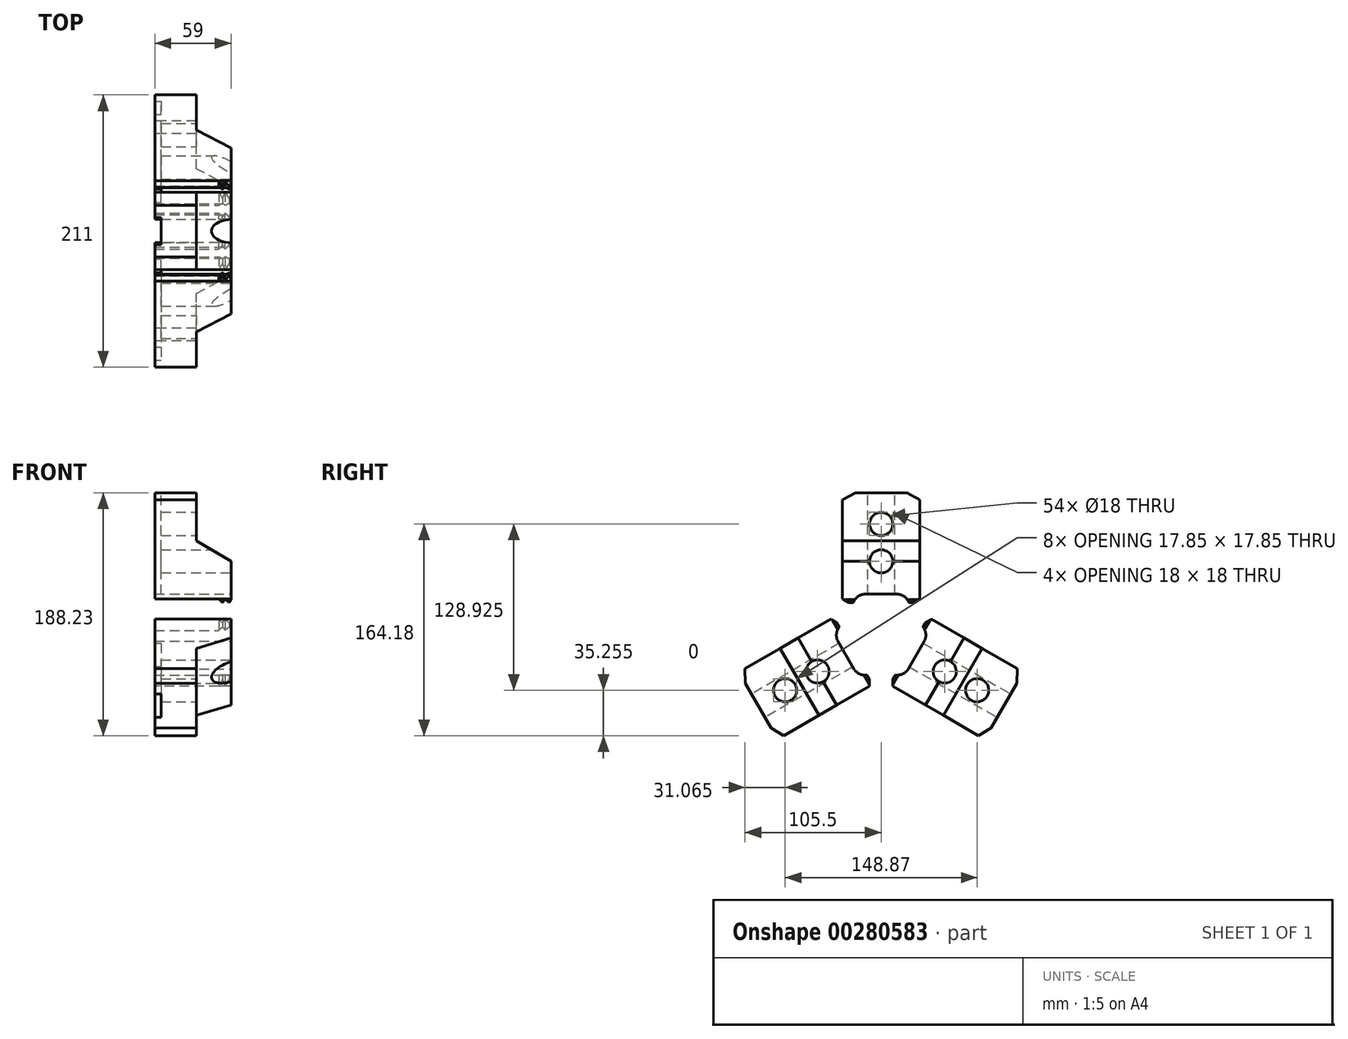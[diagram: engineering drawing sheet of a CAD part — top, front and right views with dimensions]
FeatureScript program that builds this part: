
annotation { "Feature Type Name" : "Feature", "Feature Type Description" : "" }
export const myFeature = defineFeature(function(context is Context, id is Id, definition is map)
    precondition{}
    {
        {
            var Q0;
            Q0=qCreatedBy(makeId("Right.planeOp"),FACE);
            var sketch = newSketch(context, id + "F0", { "sketchPlane" : qUnion([Q0])});
            skLineSegment(sketch, "E0", {"start": v(0, 137.35) * mm, "end": v(0, 0) * mm, "construction": true});
            skLineSegment(sketch, "E1", {"start": v(0, 25) * mm, "end": v(25, 25) * mm});
            skLineSegment(sketch, "E2", {"start": v(25, 25) * mm, "end": v(30, 27.7) * mm});
            skLineSegment(sketch, "E3", {"start": v(30, 27.7) * mm, "end": v(30, 104.5) * mm});
            skLineSegment(sketch, "E4", {"start": v(30, 104.5) * mm, "end": v(20, 110) * mm});
            skLineSegment(sketch, "E5", {"start": v(20, 110) * mm, "end": v(0, 110) * mm});
            skLineSegment(sketch, "E6", {"start": v(0, 110) * mm, "end": v(-20, 110) * mm});
            skLineSegment(sketch, "E7", {"start": v(-20, 110) * mm, "end": v(-30, 104.5) * mm});
            skLineSegment(sketch, "E8", {"start": v(-30, 104.5) * mm, "end": v(-30, 27.7) * mm});
            skLineSegment(sketch, "E9", {"start": v(-30, 27.7) * mm, "end": v(-25, 25) * mm});
            skLineSegment(sketch, "E10", {"start": v(-25, 25) * mm, "end": v(0, 25) * mm});
            skCircle(sketch, "E11", {"center": v(0, 0) * mm, "radius": 25 * mm, "construction": true});
            skSolve(sketch);
        }
        {
            var Q0;
            Q0 = qSketchRegion(id + "F0", true);
            extrude(context, id + "F1", {"entities" : qUnion([Q0]), "depth" : 62 * mm, "hasSecondDirection" : true, "secondDirectionOppositeDirection" : false, "secondDirectionDepth" : 3 * mm});
        }
        {
            var Q0;
            Q0=makeQuery(id+"F1.opExtrude","SWEPT_FACE",FACE,{"disambiguationData":[OSD([sQuery(id+"F0.wireOp",EDGE,"E8")])]});
            var sketch = newSketch(context, id + "F2", { "sketchPlane" : qUnion([Q0])});
            skLineSegment(sketch, "E12", {"start": v(35, 110) * mm, "end": v(35, 73) * mm});
            skLineSegment(sketch, "E13", {"start": v(35, 73) * mm, "end": v(62, 57) * mm});
            skLineSegment(sketch, "E14", {"start": v(62, 57) * mm, "end": v(62, 110) * mm});
            skLineSegment(sketch, "E15", {"start": v(62, 110) * mm, "end": v(35, 110) * mm});
            skLineSegment(sketch, "E16", {"start": v(3, 27.7) * mm, "end": v(52.5, 27.7) * mm});
            skLineSegment(sketch, "E17", {"start": v(52.5, 27.7) * mm, "end": v(55.5, 25) * mm});
            skLineSegment(sketch, "E18", {"start": v(55.5, 25) * mm, "end": v(57.5, 27.7) * mm});
            skLineSegment(sketch, "E19", {"start": v(57.5, 27.7) * mm, "end": v(60.5, 25) * mm});
            skLineSegment(sketch, "E20", {"start": v(60.5, 25) * mm, "end": v(62, 27) * mm});
            skLineSegment(sketch, "E21", {"start": v(62, 27) * mm, "end": v(62, 25) * mm});
            skLineSegment(sketch, "E22", {"start": v(62, 25) * mm, "end": v(3, 25) * mm});
            skLineSegment(sketch, "E23", {"start": v(3, 25) * mm, "end": v(3, 27.7) * mm});
            skSolve(sketch);
        }
        {
            var Q0;
            Q0 = qSketchRegion(id + "F2", true);
            var Q1;
            Q1=makeQuery(id+"F1.opExtrude","SWEPT_FACE",FACE,{"disambiguationData":[OSD([sQuery(id+"F0.wireOp",EDGE,"E3")])]});
            extrude(context, id + "F3", {"entities" : qUnion([Q0]), "operationType" : NewBodyOperationType.REMOVE, "endBound" : BoundingType.UP_TO_SURFACE, "oppositeDirection" : true, "endBoundEntityFace" : qUnion([Q1]), "depth" : 25 * mm});
        }
        {
            var Q0;
            Q0=makeQuery(id+"F1.opExtrude","SWEPT_FACE",FACE,{"disambiguationData":[OSD([sQuery(id+"F0.wireOp",EDGE,"E5"),sQuery(id+"F0.wireOp",EDGE,"E6")])]});
            var sketch = newSketch(context, id + "F4", { "sketchPlane" : qUnion([Q0])});
            skLineSegment(sketch, "E24", {"start": v(3, 0) * mm, "end": v(3, -10.5) * mm});
            skLineSegment(sketch, "E25", {"start": v(3, -10.5) * mm, "end": v(8, -10.5) * mm});
            skLineSegment(sketch, "E26", {"start": v(8, -10.5) * mm, "end": v(8, 0) * mm});
            skLineSegment(sketch, "E27", {"start": v(8, 0) * mm, "end": v(8, 10.5) * mm});
            skLineSegment(sketch, "E28", {"start": v(8, 10.5) * mm, "end": v(3, 10.5) * mm});
            skLineSegment(sketch, "E29", {"start": v(3, 10.5) * mm, "end": v(3, 0) * mm});
            skSolve(sketch);
        }
        {
            var Q0;
            Q0=makeQuery(id+"F4.imprint","IMPRINT",FACE,{"disambiguationData":[TD([[makeQuery(id+"F4.imprint","IMPRINT",EDGE,{"derivedFrom":sQuery(id+"F4.wireOp",EDGE,"E24")}),1.0]])]});
            var Q1;
            Q1=makeQuery(id+"F3.boolean.opBoolean","COPY",FACE,{"derivedFrom":makeQuery(id+"F3.opExtrude","SWEPT_FACE",FACE,{"disambiguationData":[OSD([sQuery(id+"F2.wireOp",EDGE,"E16")])]})});
            extrude(context, id + "F5", {"entities" : qUnion([Q0]), "operationType" : NewBodyOperationType.REMOVE, "endBound" : BoundingType.UP_TO_SURFACE, "oppositeDirection" : true, "endBoundEntityFace" : qUnion([Q1]), "depth" : 25 * mm});
        }
        {
            var Q0;
            Q0=makeQuery(id+"F1.opExtrude","CAP_FACE",FACE,{"disambiguationData":[OSD([sQuery(id+"F0.wireOp",EDGE,"E1"),sQuery(id+"F0.wireOp",EDGE,"E2"),sQuery(id+"F0.wireOp",EDGE,"E3"),sQuery(id+"F0.wireOp",EDGE,"E4"),sQuery(id+"F0.wireOp",EDGE,"E5"),sQuery(id+"F0.wireOp",EDGE,"E6"),sQuery(id+"F0.wireOp",EDGE,"E7"),sQuery(id+"F0.wireOp",EDGE,"E8"),sQuery(id+"F0.wireOp",EDGE,"E9"),sQuery(id+"F0.wireOp",EDGE,"E10")])],"isStart":false});
            var sketch = newSketch(context, id + "F6", { "sketchPlane" : qUnion([Q0])});
            skLineSegment(sketch, "E30", {"start": v(21.5, 25) * mm, "end": v(21.5, 31.5) * mm});
            skLineSegment(sketch, "E31", {"start": v(21.5, 31.5) * mm, "end": v(0, 31.5) * mm});
            skPoint(sketch, "E31.endSnap0", {"position": v(0, 27) * mm});
            skLineSegment(sketch, "E32", {"start": v(0, 31.5) * mm, "end": v(-21.5, 31.5) * mm});
            skLineSegment(sketch, "E33", {"start": v(-21.5, 31.5) * mm, "end": v(-21.5, 25) * mm});
            skLineSegment(sketch, "E34", {"start": v(-21.5, 25) * mm, "end": v(0, 25) * mm});
            skLineSegment(sketch, "E35", {"start": v(0, 25) * mm, "end": v(21.5, 25) * mm});
            skArc(sketch, "E36", {"start": v(21.5, 25) * mm, "mid": v(17.98, 29.61) * mm, "end": v(12.5, 31.5) * mm});
            skPoint(sketch, "E36.first.point", {"position": v(12.5, 31.5) * mm});
            skLineSegment(sketch, "E37", {"start": v(0, 0) * mm, "end": v(0, 113.9) * mm, "construction": true});
            skArc(sketch, "E38.MirrorCS", {"start": v(-21.5, 25) * mm, "mid": v(-17.98, 29.61) * mm, "end": v(-12.5, 31.5) * mm});
            skCircle(sketch, "E39", {"center": v(0, 85.95) * mm, "radius": 13.25 * mm});
            skCircle(sketch, "E40", {"center": v(0, 56.95) * mm, "radius": 13.25 * mm});
            skCircle(sketch, "E41", {"center": v(0, 85.95) * mm, "radius": 9 * mm});
            skCircle(sketch, "E42", {"center": v(0, 56.95) * mm, "radius": 9 * mm});
            skSolve(sketch);
        }
        {
            var Q0;
            Q0=makeQuery(id+"F6.imprint","IMPRINT",FACE,{"disambiguationData":[TD([[makeQuery(id+"F6.imprint","IMPRINT",EDGE,{"derivedFrom":sQuery(id+"F6.wireOp",EDGE,"E41")}),1.0]])]});
            var Q1;
            {var subQ0=sQuery(id+"F6.wireOp",EDGE,"E42");var subQ1=makeQuery(id+"F3.boolean.opBoolean","COPY",EDGE,{"derivedFrom":makeQuery(id+"F3.opExtrude","SWEPT_EDGE",EDGE,{"disambiguationData":[OSD([sQuery(id+"F0.wireOp",EDGE,"E8"),sQuery(id+"F2.wireOp",EDGE,"E13"),sQuery(id+"F2.wireOp",EDGE,"E14")])]})});var subQ2=makeQuery(id+"F6.imprint","INTERSECT",VERTEX,{"disambiguationData":[OD(0.0)],"derivedFrom":[subQ1,subQ0]});Q1=makeQuery(id+"F6.imprint","IMPRINT",FACE,{"disambiguationData":[TD([[makeQuery(id+"F6.imprint","IMPRINT",EDGE,{"disambiguationData":[TD([[subQ2,1.0]])],"derivedFrom":subQ0}),1.0]])]});}
            var Q2;
            {var subQ0=sQuery(id+"F6.wireOp",EDGE,"E42");var subQ1=makeQuery(id+"F3.boolean.opBoolean","COPY",EDGE,{"derivedFrom":makeQuery(id+"F3.opExtrude","SWEPT_EDGE",EDGE,{"disambiguationData":[OSD([sQuery(id+"F0.wireOp",EDGE,"E8"),sQuery(id+"F2.wireOp",EDGE,"E13"),sQuery(id+"F2.wireOp",EDGE,"E14")])]})});var subQ2=makeQuery(id+"F6.imprint","INTERSECT",VERTEX,{"disambiguationData":[OD(0.0)],"derivedFrom":[subQ1,subQ0]});Q2=makeQuery(id+"F6.imprint","IMPRINT",FACE,{"disambiguationData":[TD([[makeQuery(id+"F6.imprint","IMPRINT",EDGE,{"disambiguationData":[TD([[subQ2,-1.0]])],"derivedFrom":subQ0}),1.0]])]});}
            var Q3;
            {var subQ1=sQuery(id+"F6.wireOp",EDGE,"E31");var subQ5=sQuery(id+"F6.wireOp",EDGE,"E32");var subQ6=makeQuery(id+"F6.imprint","INTERSECT",VERTEX,{"derivedFrom":[subQ1,subQ5]});Q3=makeQuery(id+"F6.imprint","IMPRINT",FACE,{"disambiguationData":[TD([[makeQuery(id+"F6.imprint","IMPRINT",EDGE,{"disambiguationData":[TD([[subQ6,1.0]])],"derivedFrom":subQ1}),1.0]])]});}
            var Q4;
            {var subQ1=sQuery(id+"F6.wireOp",EDGE,"E34");Q4=makeQuery(id+"F6.imprint","IMPRINT",FACE,{"disambiguationData":[TD([[makeQuery(id+"F6.imprint","IMPRINT",EDGE,{"derivedFrom":subQ1}),1.0]])]});}
            var Q5;
            {var subQ0=sQuery(id+"F0.wireOp",EDGE,"E6");var subQ1=sQuery(id+"F0.wireOp",EDGE,"E5");var subQ2=sQuery(id+"F0.wireOp",EDGE,"E4");var subQ3=sQuery(id+"F0.wireOp",EDGE,"E3");Q5=makeQuery(id+"F5.boolean.opBoolean","SPLIT",FACE,{"disambiguationData":[TD([makeQuery(id+"F1.opExtrude","SWEPT_FACE",FACE,{"disambiguationData":[OSD([subQ3])]})])],"derivedFrom":makeQuery(id+"F1.opExtrude","CAP_FACE",FACE,{"disambiguationData":[OSD([sQuery(id+"F0.wireOp",EDGE,"E1"),sQuery(id+"F0.wireOp",EDGE,"E2"),subQ3,subQ2,subQ1,subQ0,sQuery(id+"F0.wireOp",EDGE,"E7"),sQuery(id+"F0.wireOp",EDGE,"E8"),sQuery(id+"F0.wireOp",EDGE,"E9"),sQuery(id+"F0.wireOp",EDGE,"E10")])],"isStart":true})});}
            extrude(context, id + "F7", {"entities" : qUnion([Q0, Q1, Q2, Q3, Q4]), "operationType" : NewBodyOperationType.REMOVE, "endBound" : BoundingType.UP_TO_SURFACE, "oppositeDirection" : true, "endBoundEntityFace" : qUnion([Q5]), "depth" : 25 * mm});
        }
        {
            var Q0;
            Q0=qCreatedBy(makeId("Front.planeOp"),FACE);
            var sketch = newSketch(context, id + "F8", { "sketchPlane" : qUnion([Q0])});
            skLineSegment(sketch, "E43", {"start": v(0, 0) * mm, "end": v(88.19, 0) * mm, "construction": true});
            skSolve(sketch);
        }
        {
            var Q0;
            Q0=makeQuery(id+"F1.opExtrude","SWEPT_BODY",BODY,{"disambiguationData":[OSD([sQuery(id+"F0.wireOp",EDGE,"E1"),sQuery(id+"F0.wireOp",EDGE,"E2"),sQuery(id+"F0.wireOp",EDGE,"E3"),sQuery(id+"F0.wireOp",EDGE,"E4"),sQuery(id+"F0.wireOp",EDGE,"E5"),sQuery(id+"F0.wireOp",EDGE,"E6"),sQuery(id+"F0.wireOp",EDGE,"E7"),sQuery(id+"F0.wireOp",EDGE,"E8"),sQuery(id+"F0.wireOp",EDGE,"E9"),sQuery(id+"F0.wireOp",EDGE,"E10")])]});
            var Q1;
            Q1=sQuery(id+"F8.wireOp",EDGE,"E43");
            circularPattern(context, id + "F9", {"entities" : qUnion([Q0]), "axis" : qUnion([Q1]), "angle" : 360 * degree, "instanceCount" : 3, "equalSpace" : true, "computeTransformsWithoutBuiltin" : true});
        }
    });
